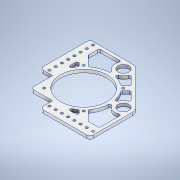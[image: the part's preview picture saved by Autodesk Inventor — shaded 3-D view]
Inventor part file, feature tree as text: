
AUTODESK INVENTOR PART (.ipt)
format: ipt  version: 2020 (Build 240168000, 168)  size: 456,192 bytes
history: native  units: in
note: dims shown in document units (in); Inventor stores cm internally (conversion verified against a paired STEP export)
features: sketch x5, extrude x4, hole x2, fillet x1
ambient origin geometry x8: Origin, YZ Plane, XZ Plane, XY Plane, X Axis, Y Axis, Z Axis, Center Point
bodies: Solid1 (feature_tree)
feature tree (12):
  extrude  "Extrusion1"  Depth=0.25in TaperAngle=0.0deg
  hole  "Hole1"  [1 undecoded]
  extrude  "Extrusion3"  Depth=4.5in
  extrude  "Extrusion4"  Depth=1.0in
  hole  "Hole2"  [1 undecoded]
  extrude  "Extrusion6"  Depth=1.0in
  fillet  "Fillet7"  [1 undecoded]
  sketch  "Sketch1"  dims[d0=3.75in d1=0.25in d2=0.0in]
  sketch  "Sketch2"  dims[d3=1.0in d4=1.0in]
  sketch  "Sketch4"  dims[d5=4.25in d9=4.5in]
  sketch  "Sketch6"  dims[d10=0.196in d11=0.75in d12=0.5in d13=0.188in d14=0.5635in d15=1.0in d16=0.8108in d26=1.0in]
  sketch  "Sketch8"  dims[d27=2.75in d28=1.75in d29=1.0in d30=0.0in d31=0.0in d37=0.875in d38=5.9094in d41=0.0in d42=0.0in d43=0.6in d44=1.8in d46=2.0in d47=2.3622in d48=6.5in d49=0.5in d50=0.5in d51=5.5118in d53=0.5in d54=0.3937in d56=1.0in d58=5.5118in d60=0.5in d61=0.3937in d63=1.0in d65=0.196in d66=0.75in d67=0.3125in d68=1.0in d69=0.5635in d70=1.0in d71=0.8108in d72=0.75in d94=1.375in d96=1.0in d97=0.0in d98=0.125in d99=0.25in d101=0.25in d102=0.25in d103=0.25in d105=0.25in d108=0.25in d109=0.25in d111=0.25in d113=0.25in d114=0.25in]
note: 3 required parameter values undecoded (feature->parameter linkage not recoverable at this tier; creation-order binding heuristic only, values carry confidence <= 0.55)
